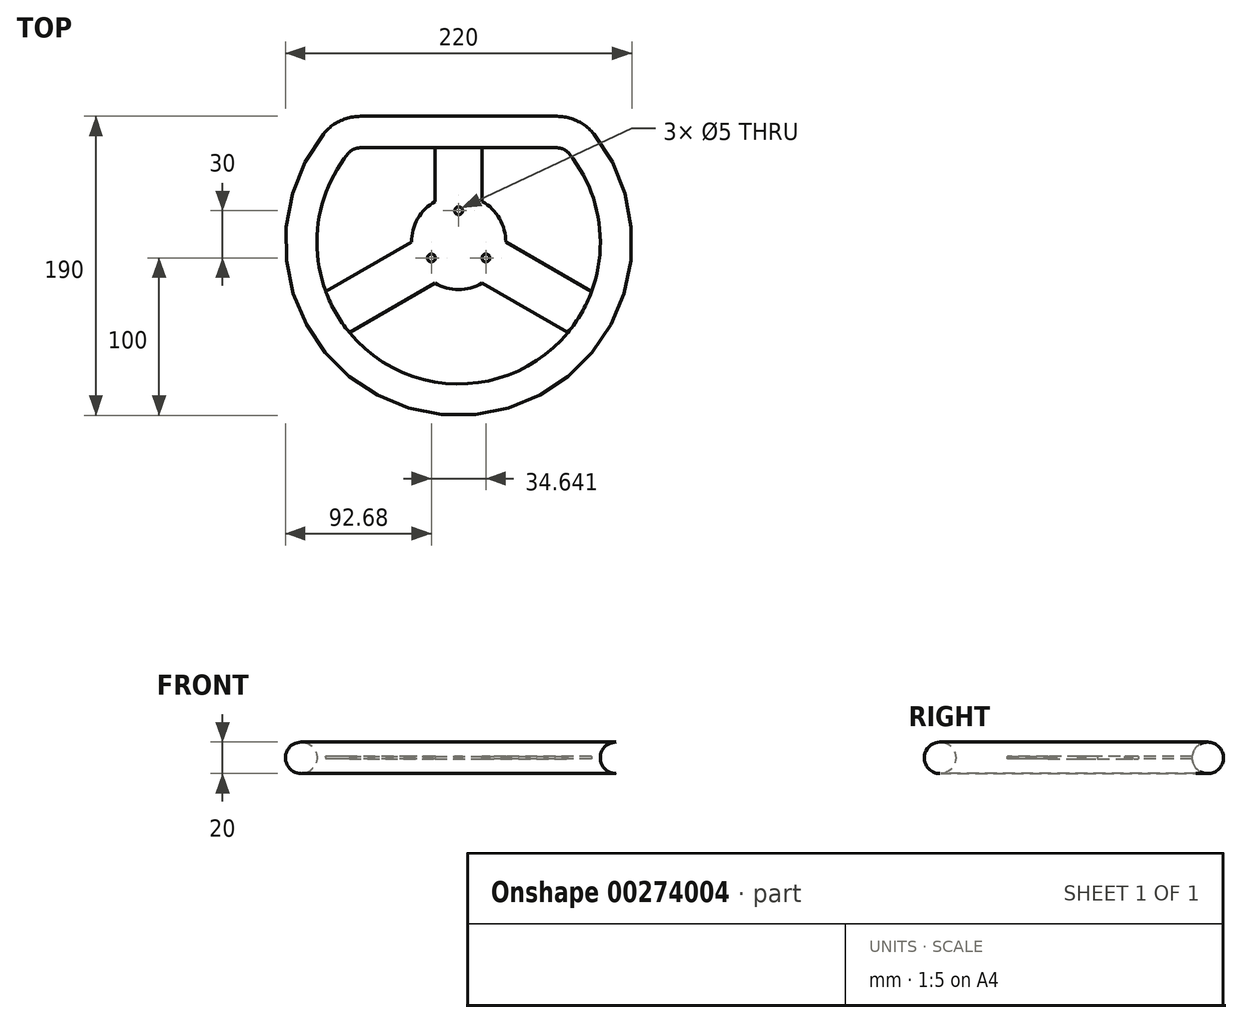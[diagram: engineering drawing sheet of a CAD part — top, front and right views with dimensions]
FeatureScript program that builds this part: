
annotation { "Feature Type Name" : "Feature", "Feature Type Description" : "" }
export const myFeature = defineFeature(function(context is Context, id is Id, definition is map)
    precondition{}
    {
        {
            var Q0;
            Q0=qCreatedBy(makeId("Top.planeOp"),FACE);
            var sketch = newSketch(context, id + "F0", { "sketchPlane" : qUnion([Q0])});
            skCircle(sketch, "E0", {"center": v(0, 0) * mm, "radius": 100 * mm, "construction": true});
            skLineSegment(sketch, "E1", {"start": v(-71.41, 70) * mm, "end": v(71.41, 70) * mm, "construction": true});
            skCircle(sketch, "E2", {"center": v(0, 0) * mm, "radius": 30 * mm});
            skLineSegment(sketch, "E3", {"start": v(-15, 70) * mm, "end": v(-15, 25.98) * mm});
            skLineSegment(sketch, "E4", {"start": v(15, 70) * mm, "end": v(15, 25.98) * mm});
            skLineSegment(sketch, "E5", {"start": v(-15, 70) * mm, "end": v(15, 70) * mm});
            skLineSegment(sketch, "E6", {"start": v(-30, 0) * mm, "end": v(-93.12, -36.44) * mm});
            skLineSegment(sketch, "E7", {"start": v(-93.12, -36.44) * mm, "end": v(-78.12, -62.42) * mm});
            skLineSegment(sketch, "E8", {"start": v(-78.12, -62.42) * mm, "end": v(-15, -25.98) * mm});
            skLineSegment(sketch, "E9", {"start": v(15, -25.98) * mm, "end": v(78.12, -62.42) * mm});
            skLineSegment(sketch, "E10", {"start": v(78.12, -62.42) * mm, "end": v(93.12, -36.44) * mm});
            skLineSegment(sketch, "E11", {"start": v(93.12, -36.44) * mm, "end": v(30, 0) * mm});
            skSolve(sketch);
        }
        {
            var Q0;
            Q0=qSketchRegion(id+"F0",true);
            extrude(context, id + "F1", {"entities" : qUnion([Q0]), "endBound" : BoundingType.SYMMETRIC, "depth" : 1.6 * mm});
        }
        {
            var Q0;
            Q0=makeQuery(id+"F1.opExtrude","CAP_FACE",FACE,{"disambiguationData":[OSD([sQuery(id+"F0.wireOp",EDGE,"E2"),sQuery(id+"F0.wireOp",EDGE,"E3"),sQuery(id+"F0.wireOp",EDGE,"E4"),sQuery(id+"F0.wireOp",EDGE,"E5"),sQuery(id+"F0.wireOp",EDGE,"E6"),sQuery(id+"F0.wireOp",EDGE,"E7"),sQuery(id+"F0.wireOp",EDGE,"E8"),sQuery(id+"F0.wireOp",EDGE,"E9"),sQuery(id+"F0.wireOp",EDGE,"E10"),sQuery(id+"F0.wireOp",EDGE,"E11")])],"isStart":false});
            var sketch = newSketch(context, id + "F2", { "sketchPlane" : qUnion([Q0])});
            skCircle(sketch, "E12", {"center": v(0, 0) * mm, "radius": 20 * mm, "construction": true});
            skCircle(sketch, "E13", {"center": v(0, 20) * mm, "radius": 2.5 * mm});
            skCircle(sketch, "E14.1.0", {"center": v(-17.32, -10) * mm, "radius": 2.5 * mm});
            skCircle(sketch, "E14.2.0", {"center": v(17.32, -10) * mm, "radius": 2.5 * mm});
            skSolve(sketch);
        }
        {
            var Q0;
            Q0=qSketchRegion(id+"F2",true);
            extrude(context, id + "F3", {"entities" : qUnion([Q0]), "operationType" : NewBodyOperationType.REMOVE, "endBound" : BoundingType.THROUGH_ALL, "oppositeDirection" : true, "depth" : 25 * mm});
        }
        {
            var Q0;
            Q0=qCreatedBy(makeId("Top.planeOp"),FACE);
            var sketch = newSketch(context, id + "F4", { "sketchPlane" : qUnion([Q0])});
            skLineSegment(sketch, "E15.0", {"start": v(0, 70) * mm, "end": v(62.45, 70) * mm});
            skArc(sketch, "E15.1", {"start": v(0, -100) * mm, "mid": v(90.14, -43.3) * mm, "end": v(78.06, 62.5) * mm});
            skLineSegment(sketch, "E16", {"start": v(0, 100) * mm, "end": v(0, -100) * mm, "construction": true});
            skPoint(sketch, "E17.orphan", {"position": v(-71.41, 70) * mm});
            skPoint(sketch, "E18.visualSharp", {"position": v(71.41, 70) * mm});
            skArc(sketch, "E18.filletArc", {"start": v(78.06, 62.5) * mm, "mid": v(71.11, 68.03) * mm, "end": v(62.45, 70) * mm});
            skSolve(sketch);
        }
        {
            var Q0;
            Q0=qCreatedBy(makeId("Right.planeOp"),FACE);
            var sketch = newSketch(context, id + "F5", { "sketchPlane" : qUnion([Q0])});
            skPoint(sketch, "E19.0", {"position": v(70, 0) * mm});
            skCircle(sketch, "E20", {"center": v(70, 0) * mm, "radius": 10 * mm});
            skSolve(sketch);
        }
        {
            var Q0;
            Q0=makeQuery(id+"F5.imprint","IMPRINT",FACE,{"disambiguationData":[TD([[makeQuery(id+"F5.imprint","IMPRINT",EDGE,{"derivedFrom":sQuery(id+"F5.wireOp",EDGE,"E20")}),1.0]])]});
            var Q1;
            Q1=qConstructionFilter(qBodyType(qCreatedBy(id+"F4",EDGE),BodyType.WIRE),ConstructionObject.NO);
            sweep(context, id + "F6", {"profiles" : qUnion([Q0]), "path" : qUnion([Q1])});
        }
        {
            var Q0;
            Q0=makeQuery(id+"F6.opSweep","SWEPT_BODY",BODY,{"disambiguationData":[OSD([sQuery(id+"F4.wireOp",EDGE,"E15.0"),sQuery(id+"F5.wireOp",EDGE,"E20")])]});
            var Q1;
            Q1=qCreatedBy(makeId("Right.planeOp"),FACE);
            mirror(context, id + "F7", {"operationType" : NewBodyOperationType.ADD, "entities" : qUnion([Q0]), "mirrorPlane" : qUnion([Q1])});
        }
    });
